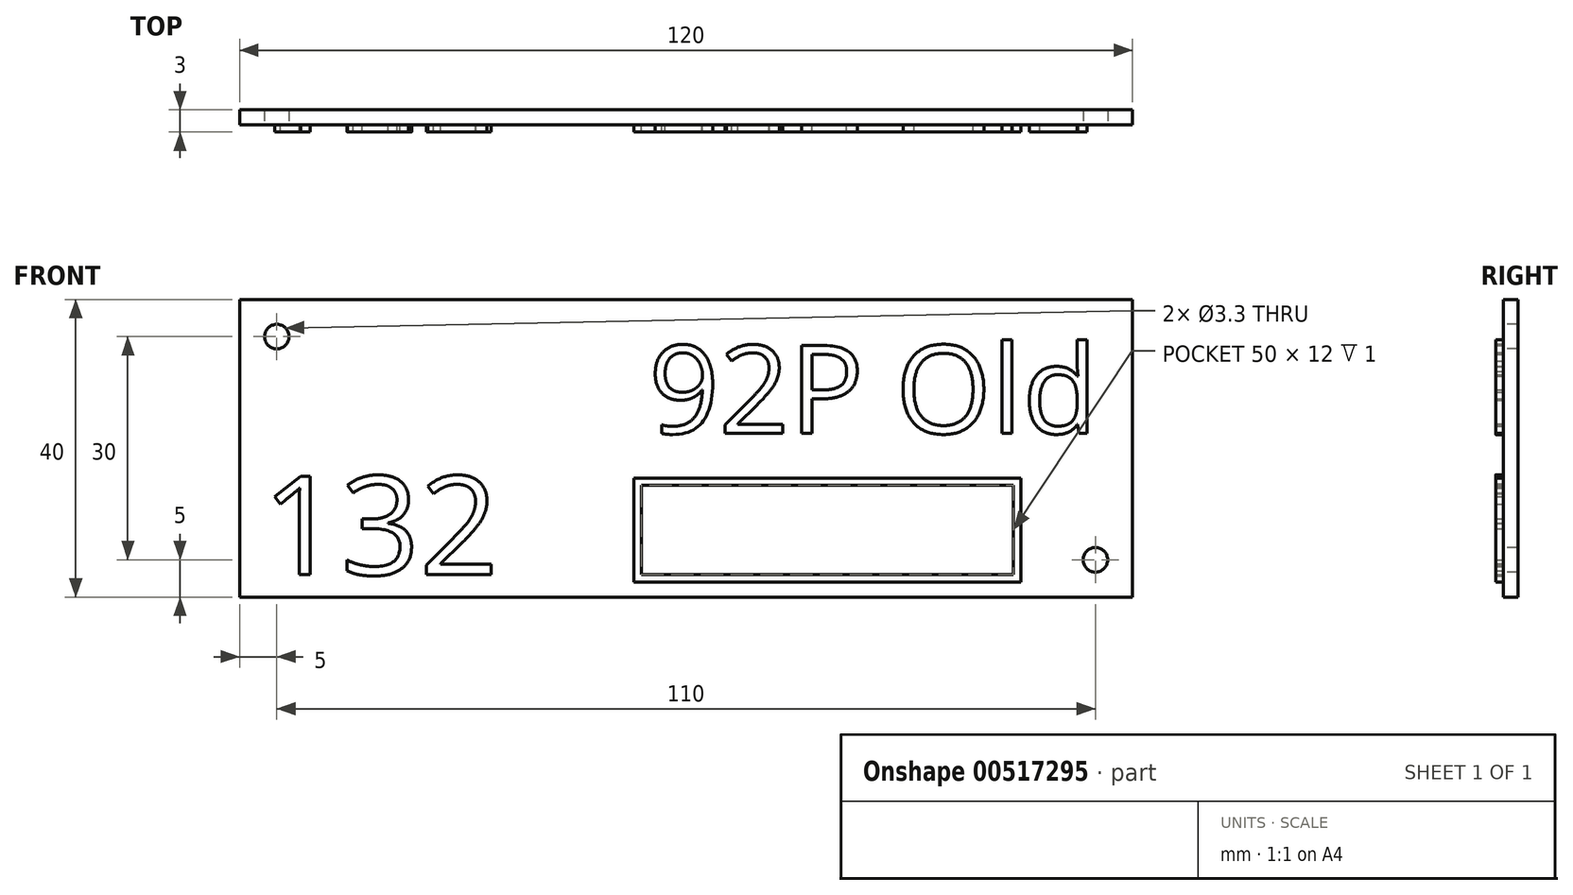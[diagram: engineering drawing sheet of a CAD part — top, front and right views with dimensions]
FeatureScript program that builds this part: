
annotation { "Feature Type Name" : "Feature", "Feature Type Description" : "" }
export const myFeature = defineFeature(function(context is Context, id is Id, definition is map)
    precondition{}
    {
        {
            var Q0;
            Q0=qCreatedBy(makeId("Front.planeOp"),FACE);
            var sketch = newSketch(context, id + "F0", { "sketchPlane" : qUnion([Q0])});
            skLineSegment(sketch, "E0.bottom", {"start": v(60, -20) * mm, "end": v(-60, -20) * mm});
            skLineSegment(sketch, "E0.top", {"start": v(60, 20) * mm, "end": v(-60, 20) * mm});
            skLineSegment(sketch, "E0.left", {"start": v(60, -20) * mm, "end": v(60, 20) * mm});
            skLineSegment(sketch, "E0.right", {"start": v(-60, -20) * mm, "end": v(-60, 20) * mm});
            skPoint(sketch, "E0.middle", {"position": v(0, 0) * mm});
            skSolve(sketch);
        }
        {
            var Q0;
            Q0=makeQuery(id+"F0.imprint","IMPRINT",FACE,{"disambiguationData":[TD([[makeQuery(id+"F0.imprint","IMPRINT",EDGE,{"derivedFrom":sQuery(id+"F0.wireOp",EDGE,"E0.bottom")}),-1.0]])]});
            extrude(context, id + "F1", {"entities" : qUnion([Q0]), "depth" : 2 * mm});
        }
        {
            var Q0;
            Q0=makeQuery(id+"F1.opExtrude","CAP_FACE",FACE,{"disambiguationData":[OSD([sQuery(id+"F0.wireOp",EDGE,"E0.bottom"),sQuery(id+"F0.wireOp",EDGE,"E0.top"),sQuery(id+"F0.wireOp",EDGE,"E0.left"),sQuery(id+"F0.wireOp",EDGE,"E0.right")])],"isStart":false});
            var sketch = newSketch(context, id + "F2", { "sketchPlane" : qUnion([Q0])});
            skPoint(sketch, "E1", {"position": v(-55, 15) * mm});
            skPoint(sketch, "E2", {"position": v(55, -15) * mm});
            skSolve(sketch);
        }
        {
            var Q0;
            Q0=sQuery(id+"F2.wireOp",VERTEX,"E1");
            var Q1;
            Q1=sQuery(id+"F2.wireOp",VERTEX,"E2");
            var Q2;
            Q2=makeQuery(id+"F1.opExtrude","SWEPT_BODY",BODY,{"disambiguationData":[OSD([sQuery(id+"F0.wireOp",EDGE,"E0.bottom"),sQuery(id+"F0.wireOp",EDGE,"E0.top"),sQuery(id+"F0.wireOp",EDGE,"E0.left"),sQuery(id+"F0.wireOp",EDGE,"E0.right")])]});
            hole(context, id + "F3", {"style" : HoleStyle.SIMPLE, "endStyle" : HoleEndStyle.THROUGH, "holeDiameter" : 3.3 * mm, "locations" : qUnion([Q0, Q1]), "scope" : qUnion([Q2]), "isTappedThrough" : true});
        }
        {
            var Q0;
            Q0=makeQuery(id+"F1.opExtrude","CAP_FACE",FACE,{"disambiguationData":[OSD([sQuery(id+"F0.wireOp",EDGE,"E0.bottom"),sQuery(id+"F0.wireOp",EDGE,"E0.top"),sQuery(id+"F0.wireOp",EDGE,"E0.left"),sQuery(id+"F0.wireOp",EDGE,"E0.right")])],"isStart":false});
            var sketch = newSketch(context, id + "F4", { "sketchPlane" : qUnion([Q0])});
            skText(sketch, "E3", { "text": "92P Old", "fontName": "OpenSans-Regular.ttf"});
            const initialGuessF4  = {"E3": [-0.005, 0.002, 1, 0, 0.0119]};
            skSetInitialGuess(sketch, initialGuessF4);
            skSolve(sketch);
        }
        {
            var Q0;
            Q0=qSketchRegion(id+"F4",true);
            extrude(context, id + "F5", {"entities" : qUnion([Q0]), "operationType" : NewBodyOperationType.ADD, "depth" : 1 * mm});
        }
        {
            var Q0;
            {var subQ0=sQuery(id+"F0.wireOp",EDGE,"E0.top");var subQ1=sQuery(id+"F0.wireOp",EDGE,"E0.left");var subQ2=sQuery(id+"F0.wireOp",EDGE,"E0.right");var subQ3=sQuery(id+"F0.wireOp",EDGE,"E0.bottom");Q0=makeQuery(id+"F5.boolean.opBoolean","SPLIT",FACE,{"disambiguationData":[TD([makeQuery(id+"F1.opExtrude","SWEPT_FACE",FACE,{"disambiguationData":[OSD([subQ3])]})])],"derivedFrom":makeQuery(id+"F1.opExtrude","CAP_FACE",FACE,{"disambiguationData":[OSD([subQ3,subQ0,subQ1,subQ2])],"isStart":false})});}
            var sketch = newSketch(context, id + "F6", { "sketchPlane" : qUnion([Q0])});
            skText(sketch, "E4", { "text": "132", "fontName": "OpenSans-Regular.ttf"});
            const initialGuessF6  = {"E4": [-0.057, -0.017, 1, 0, 0.01335]};
            skSetInitialGuess(sketch, initialGuessF6);
            skSolve(sketch);
        }
        {
            var Q0;
            Q0=qSketchRegion(id+"F6",true);
            extrude(context, id + "F7", {"entities" : qUnion([Q0]), "operationType" : NewBodyOperationType.ADD, "depth" : 1 * mm});
        }
        {
            var Q0;
            {var subQ46=sQuery(id+"F0.wireOp",EDGE,"E0.top");var subQ48=sQuery(id+"F0.wireOp",EDGE,"E0.left");var subQ66=sQuery(id+"F0.wireOp",EDGE,"E0.right");var subQ76=sQuery(id+"F0.wireOp",EDGE,"E0.bottom");var subQ77=makeQuery(id+"F1.opExtrude","SWEPT_FACE",FACE,{"disambiguationData":[OSD([subQ76])]});Q0=makeQuery(id+"F7.boolean.opBoolean","SPLIT",FACE,{"disambiguationData":[TD([subQ77])],"derivedFrom":makeQuery(id+"F5.boolean.opBoolean","SPLIT",FACE,{"disambiguationData":[TD([subQ77])],"derivedFrom":makeQuery(id+"F1.opExtrude","CAP_FACE",FACE,{"disambiguationData":[OSD([subQ76,subQ46,subQ48,subQ66])],"isStart":false})})});}
            var sketch = newSketch(context, id + "F8", { "sketchPlane" : qUnion([Q0])});
            skLineSegment(sketch, "E5.bottom", {"start": v(45, -18) * mm, "end": v(-7, -18) * mm});
            skLineSegment(sketch, "E5.top", {"start": v(45, -4) * mm, "end": v(-7, -4) * mm});
            skLineSegment(sketch, "E5.left", {"start": v(45, -18) * mm, "end": v(45, -4) * mm});
            skLineSegment(sketch, "E5.right", {"start": v(-7, -18) * mm, "end": v(-7, -4) * mm});
            skPoint(sketch, "E5.middle", {"position": v(19, -11) * mm});
            skLineSegment(sketch, "E6.0", {"start": v(44, -5) * mm, "end": v(-6, -5) * mm});
            skLineSegment(sketch, "E6.1", {"start": v(44, -17) * mm, "end": v(44, -5) * mm});
            skLineSegment(sketch, "E6.2", {"start": v(44, -17) * mm, "end": v(-6, -17) * mm});
            skLineSegment(sketch, "E6.3", {"start": v(-6, -17) * mm, "end": v(-6, -5) * mm});
            skSolve(sketch);
        }
        {
            var Q0;
            Q0=makeQuery(id+"F8.imprint","IMPRINT",FACE,{"disambiguationData":[TD([[makeQuery(id+"F8.imprint","IMPRINT",EDGE,{"derivedFrom":sQuery(id+"F8.wireOp",EDGE,"E5.bottom")}),-1.0]])]});
            extrude(context, id + "F9", {"entities" : qUnion([Q0]), "operationType" : NewBodyOperationType.ADD, "depth" : 1 * mm});
        }
    });
